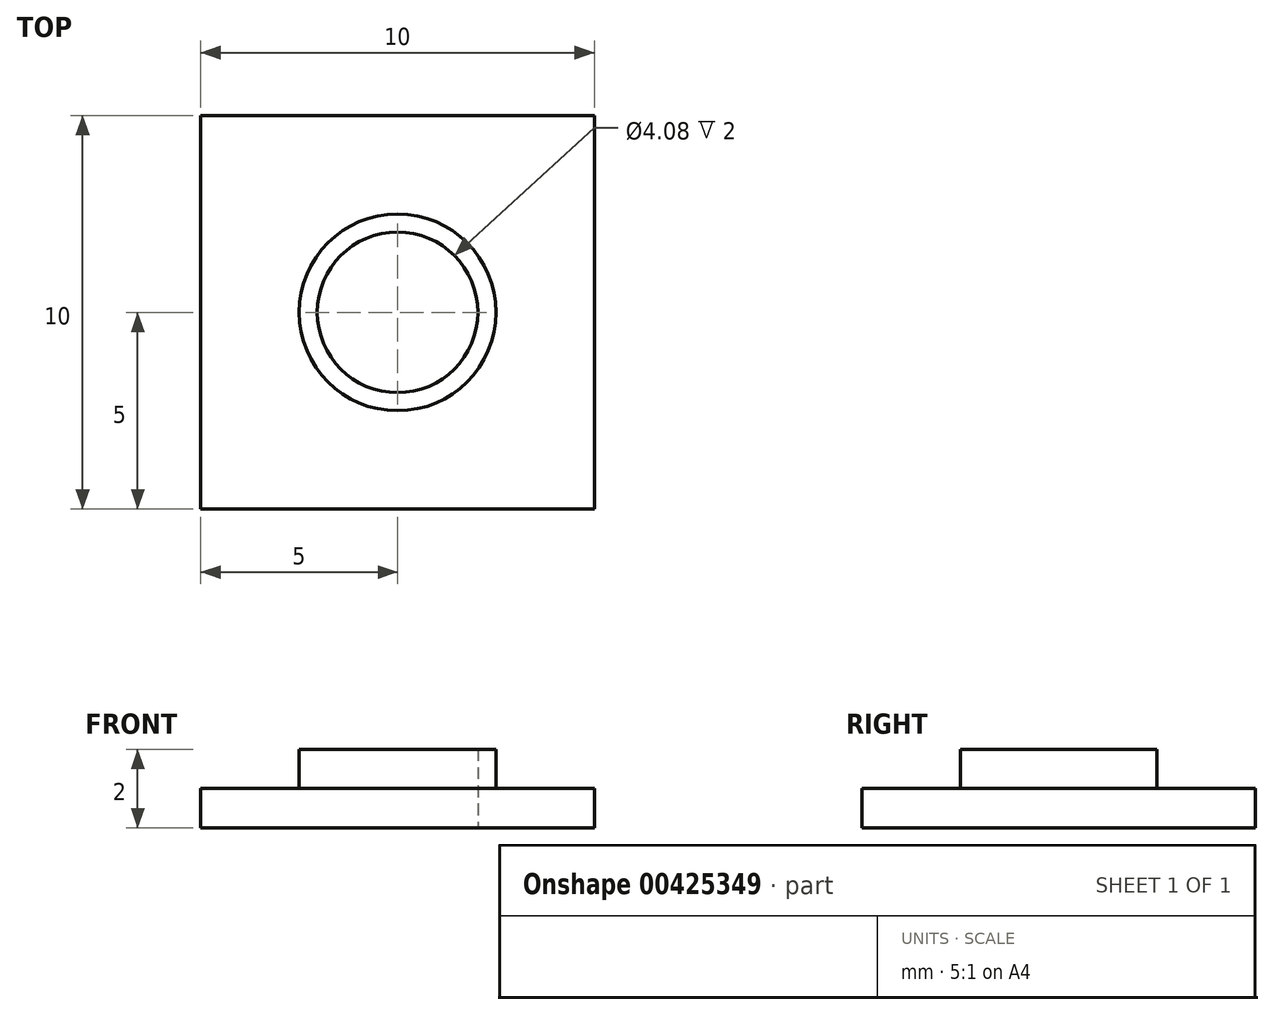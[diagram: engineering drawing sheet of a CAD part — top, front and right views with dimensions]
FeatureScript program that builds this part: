
annotation { "Feature Type Name" : "Feature", "Feature Type Description" : "" }
export const myFeature = defineFeature(function(context is Context, id is Id, definition is map)
    precondition{}
    {
        {
            var Q0;
            Q0=qCreatedBy(makeId("Top.planeOp"),FACE);
            var sketch = newSketch(context, id + "F0", { "sketchPlane" : qUnion([Q0])});
            skCircle(sketch, "E0", {"center": v(0, 0) * mm, "radius": 2.04 * mm});
            skCircle(sketch, "E1", {"center": v(0, 0) * mm, "radius": 2.5 * mm});
            skSolve(sketch);
        }
        {
            var Q0;
            Q0=makeQuery(id+"F0.imprint","IMPRINT",FACE,{"disambiguationData":[TD([[makeQuery(id+"F0.imprint","IMPRINT",EDGE,{"derivedFrom":sQuery(id+"F0.wireOp",EDGE,"E0")}),-1.0]])]});
            extrude(context, id + "F1", {"entities" : qUnion([Q0]), "depth" : 1 * mm});
        }
        {
            var Q0;
            Q0=makeQuery(id+"F1.opExtrude","CAP_FACE",FACE,{"disambiguationData":[OSD([sQuery(id+"F0.wireOp",EDGE,"E0"),sQuery(id+"F0.wireOp",EDGE,"E1")])],"isStart":true});
            var sketch = newSketch(context, id + "F2", { "sketchPlane" : qUnion([Q0])});
            skCircle(sketch, "E2", {"center": v(0, 0) * mm, "radius": 2.04 * mm});
            skCircle(sketch, "E3", {"center": v(0, 0) * mm, "radius": 5 * mm});
            skLineSegment(sketch, "E4.bottom", {"start": v(-5, -5) * mm, "end": v(5, -5) * mm});
            skLineSegment(sketch, "E4.top", {"start": v(-5, 5) * mm, "end": v(5, 5) * mm});
            skLineSegment(sketch, "E4.left", {"start": v(-5, -5) * mm, "end": v(-5, 5) * mm});
            skLineSegment(sketch, "E4.right", {"start": v(5, -5) * mm, "end": v(5, 5) * mm});
            skSolve(sketch);
        }
        {
            var Q0;
            Q0=makeQuery(id+"F2.imprint","IMPRINT",FACE,{"disambiguationData":[TD([[makeQuery(id+"F2.imprint","IMPRINT",EDGE,{"derivedFrom":sQuery(id+"F2.wireOp",EDGE,"E3")}),-1.0]])]});
            var Q1;
            Q1=makeQuery(id+"F2.imprint","IMPRINT",FACE,{"disambiguationData":[TD([[makeQuery(id+"F2.imprint","IMPRINT",EDGE,{"derivedFrom":sQuery(id+"F2.wireOp",EDGE,"E3")}),1.0]])]});
            var Q2;
            Q2=makeQuery(id+"F2.imprint","IMPRINT",FACE,{"disambiguationData":[TD([[makeQuery(id+"F2.imprint","IMPRINT",EDGE,{"derivedFrom":sQuery(id+"F2.wireOp",EDGE,"E2")}),1.0]])]});
            extrude(context, id + "F3", {"entities" : qUnion([Q0, Q1, Q2]), "operationType" : NewBodyOperationType.ADD, "depth" : 1 * mm});
        }
    });
